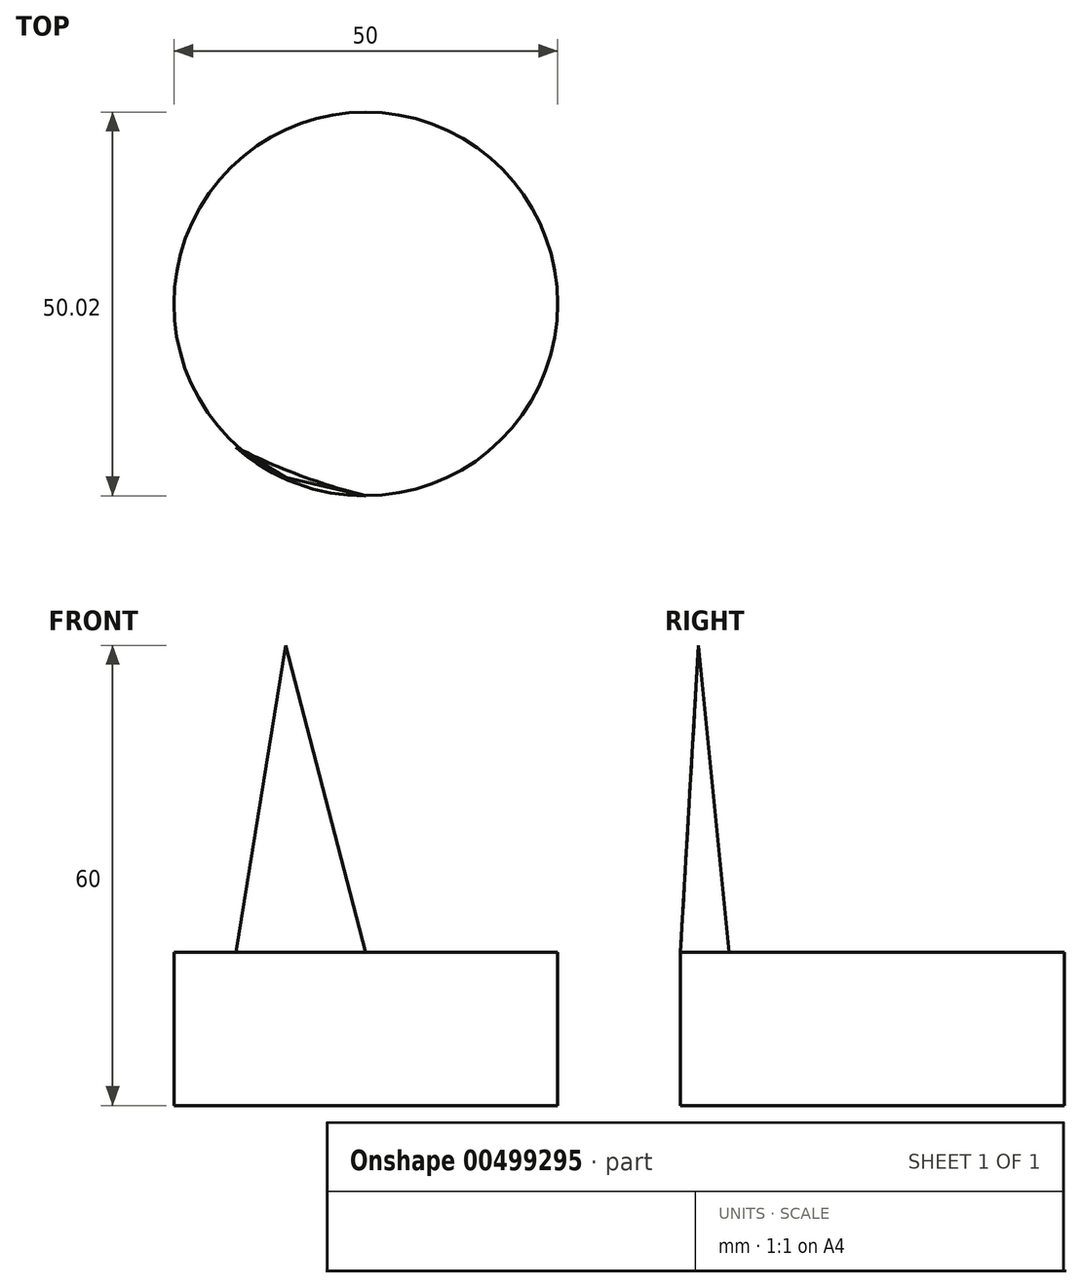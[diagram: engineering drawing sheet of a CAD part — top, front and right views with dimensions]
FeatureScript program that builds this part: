
annotation { "Feature Type Name" : "Feature", "Feature Type Description" : "" }
export const myFeature = defineFeature(function(context is Context, id is Id, definition is map)
    precondition{}
    {
        {
            var Q0;
            Q0=qCreatedBy(makeId("Top.planeOp"),FACE);
            var sketch = newSketch(context, id + "F0", { "sketchPlane" : qUnion([Q0])});
            skCircle(sketch, "E0", {"center": v(0, 0) * mm, "radius": 25 * mm});
            skSolve(sketch);
        }
        {
            var Q0;
            Q0 = qSketchRegion(id + "F0", true);
            extrude(context, id + "F1", {"entities" : qUnion([Q0]), "depth" : 20 * mm});
        }
        {
            var Q0;
            Q0=qCreatedBy(makeId("Top.planeOp"),FACE);
            cPlane(context, id + "F2", {"entities" : qUnion([Q0]), "cplaneType" : CPlaneType.OFFSET, "offset" : 20 * mm, "width" : 150 * mm, "height" : 150 * mm});
        }
        {
            var Q0;
            Q0=qCreatedBy(id+"F2.planeOp",FACE);
            var sketch = newSketch(context, id + "F3", { "sketchPlane" : qUnion([Q0])});
            skArc(sketch, "E1", {"start": v(0, 25.13) * mm, "mid": v(-9.64, 22.96) * mm, "end": v(-17.72, 17.27) * mm});
            skArc(sketch, "E2", {"start": v(0, 25.13) * mm, "mid": v(-9.16, 21.87) * mm, "end": v(-17.72, 17.27) * mm});
            skArc(sketch, "E3", {"start": v(-18.64, 16.49) * mm, "mid": v(-23.42, 8.87) * mm, "end": v(-24.92, 0) * mm});
            skArc(sketch, "E4", {"start": v(-18.64, 16.49) * mm, "mid": v(-22.62, 8.56) * mm, "end": v(-24.92, 0) * mm});
            skArc(sketch, "E5", {"start": v(-24.92, -1.02) * mm, "mid": v(-23.1, -10.13) * mm, "end": v(-17.72, -17.71) * mm});
            skArc(sketch, "E6", {"start": v(-24.92, -1.02) * mm, "mid": v(-22.2, -9.75) * mm, "end": v(-17.72, -17.71) * mm});
            skArc(sketch, "E7", {"start": v(-16.94, -18.7) * mm, "mid": v(-9.05, -23.42) * mm, "end": v(0, -25.02) * mm});
            skArc(sketch, "E8", {"start": v(-16.94, -18.7) * mm, "mid": v(-8.65, -22.34) * mm, "end": v(0, -25.02) * mm});
            skArc(sketch, "E9", {"start": v(1.2, -25.02) * mm, "mid": v(9.69, -23.42) * mm, "end": v(16.92, -18.7) * mm});
            skArc(sketch, "E10", {"start": v(1.2, -25.02) * mm, "mid": v(9.37, -22.63) * mm, "end": v(16.92, -18.7) * mm});
            skArc(sketch, "E11", {"start": v(17.61, -17.71) * mm, "mid": v(23.6, -9.8) * mm, "end": v(25.16, 0) * mm});
            skArc(sketch, "E12", {"start": v(17.61, -17.71) * mm, "mid": v(22.9, -9.5) * mm, "end": v(25.16, 0) * mm});
            skArc(sketch, "E13", {"start": v(25.16, 0.87) * mm, "mid": v(23.6, 9.36) * mm, "end": v(18.74, 16.49) * mm});
            skArc(sketch, "E14", {"start": v(25.16, 0.87) * mm, "mid": v(22.55, 8.92) * mm, "end": v(18.74, 16.49) * mm});
            skArc(sketch, "E15", {"start": v(17.96, 17.28) * mm, "mid": v(10.36, 22.94) * mm, "end": v(1.12, 25) * mm});
            skArc(sketch, "E16", {"start": v(17.96, 17.28) * mm, "mid": v(9.96, 22.05) * mm, "end": v(1.12, 25) * mm});
            skSolve(sketch);
        }
        {
            var Q0;
            Q0=qCreatedBy(id+"F2.planeOp",FACE);
            cPlane(context, id + "F4", {"entities" : qUnion([Q0]), "cplaneType" : CPlaneType.OFFSET, "offset" : 40 * mm, "width" : 150 * mm, "height" : 150 * mm});
        }
        {
            var Q0;
            Q0=qCreatedBy(id+"F4.planeOp",FACE);
            var sketch = newSketch(context, id + "F5", { "sketchPlane" : qUnion([Q0])});
            skCircle(sketch, "E17", {"center": v(-9.1, 23.1) * mm, "radius": 0.68 * mm});
            skCircle(sketch, "E18", {"center": v(-23.02, 9.7) * mm, "radius": 0.77 * mm});
            skCircle(sketch, "E19", {"center": v(10.46, 22.8) * mm, "radius": 0.75 * mm});
            skCircle(sketch, "E20", {"center": v(22.47, 10.74) * mm, "radius": 0.65 * mm});
            skCircle(sketch, "E21", {"center": v(22.33, -10.51) * mm, "radius": 0.6 * mm});
            skCircle(sketch, "E22", {"center": v(-23.24, -9.76) * mm, "radius": 0.59 * mm});
            skCircle(sketch, "E23", {"center": v(-10.43, -22.66) * mm, "radius": 0.96 * mm});
            skCircle(sketch, "E24", {"center": v(9.08, -22.9) * mm, "radius": 0.94 * mm});
            skSolve(sketch);
        }
        {
            var Q1;
            Q1=makeQuery(id+"F3.imprint","IMPRINT",FACE,{"disambiguationData":[TD([[makeQuery(id+"F3.imprint","IMPRINT",EDGE,{"derivedFrom":sQuery(id+"F3.wireOp",EDGE,"E7")}),1.0]])]});
            var Q2;
            Q2=sQuery(id+"F5.wireOp",VERTEX,"E23.center");
            loft(context, id + "F6", {"operationType" : NewBodyOperationType.ADD, "sheetProfilesArray" : [{ "sheetProfileEntities" : qUnion([Q1]) }, { "sheetProfileEntities" : qUnion([Q2]) }]});
        }
    });
